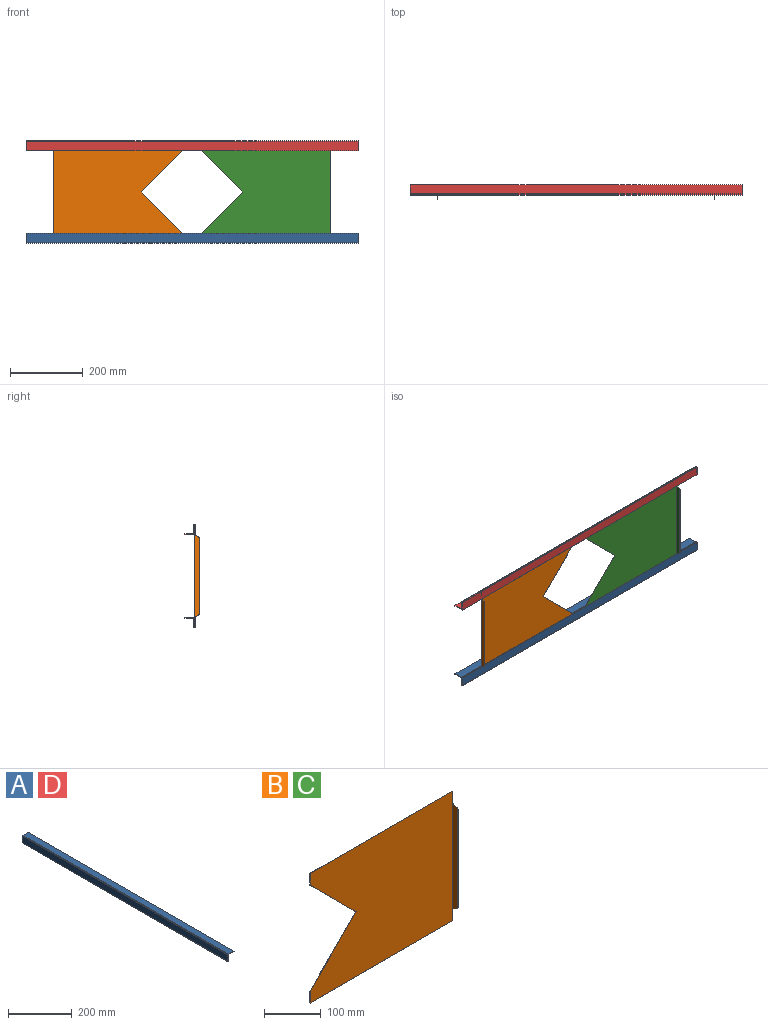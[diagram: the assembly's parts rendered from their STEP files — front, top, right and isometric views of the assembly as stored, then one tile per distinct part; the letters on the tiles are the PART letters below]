
ASSEMBLY  parts=4 mates=9
PART A: 15 faces, bbox 28.3x914.4x27 mm
  f0: plane 914.4x1.59mm, normal (1,0,0), area 1451.6mm2, adj f1,f9,f10,f11
  f1: plane 914.4x23.88mm, normal (0,0,1), area 21832.2mm2, adj f0,f10,f11,f14
  f2: plane 914.4x23.88mm, normal (-1,0,0), area 21832.2mm2, adj f3,f10,f11,f14
  f3: plane 914.4x1.27mm, normal (0,0,1), area 1161.3mm2, adj f2,f4,f10,f11
  f4: plane 914.4x25.4mm, normal (1,0,0), area 23225.8mm2, adj f3,f5,f10,f11
  f5: plane 914.4x1.59mm, normal (0,0,1), area 1451.6mm2, adj f4,f6,f10,f11
  f6: plane 914.4x25.46mm, normal (-1,0,0), area 23283.8mm2, adj f5,f10,f11,f13
  f7: plane 914.4x1.4mm, normal (0,0,-1), area 1277.4mm2, adj f10,f11,f12,f13
  f8: plane 914.4x23.88mm, normal (1,0,0), area 21832.2mm2, adj f9,f10,f11,f12
  f9: plane 914.4x23.81mm, normal (0,0,-1), area 21774.1mm2, adj f0,f8,f10,f11
  f10: plane 28.26x26.99mm, normal (0,-1,0), area 124mm2, adj f0,f1,f2,f3,f4,f5,f6,f7
  f11: plane 28.26x26.99mm, normal (0,1,0), area 124mm2, adj f0,f1,f2,f3,f4,f5,f6,f7
  f12: cylinder r=1.52mm len=914.4mm, axis (0,1,0), area 2189mm2, adj f7,f8,f10,f11
  f13: cylinder r=1.52mm len=914.4mm, axis (0,1,0), area 2189mm2, adj f6,f7,f10,f11
  f14: cylinder r=1.52mm len=914.4mm, axis (0,1,0), area 2189mm2, adj f1,f2,f10,f11
PART B: 16 faces, bbox 355.6x13.3x279.4 mm
  f0: plane 228.6x12.7mm, normal (1,0,0), area 2819.2mm2, adj f1,f11,f12,f13,f14,f15
  f1: plane 209.62x0.55mm, normal (0,-1,0), area 115.5mm2, adj f0,f2,f14,f15
  f2: plane 228.6x12.7mm, normal (-1,0,0), area 2819.2mm2, adj f1,f3,f12,f13,f14,f15
  f3: plane 355.6x279.4mm, normal (0,-1,0), area 86164.2mm2, adj f2,f4,f5,f6,f7,f8,f9,f11
  f4: plane 355.6x0.55mm, normal (0,0,-1), area 195.9mm2, adj f3,f9,f10,f11
  f5: plane 355.6x0.55mm, normal (0,0,1), area 195.9mm2, adj f3,f6,f10,f11
  f6: plane 25.4x0.55mm, normal (-1,0,0), area 14mm2, adj f3,f5,f7,f10
  f7: plane 114.3x114.3mm, normal (-0.71,0,-0.71), area 89.1mm2, adj f3,f6,f8,f10
  f8: plane 114.3x114.3mm, normal (-0.71,0,0.71), area 89.1mm2, adj f3,f7,f9,f10
  f9: plane 25.4x0.55mm, normal (-1,0,0), area 14mm2, adj f3,f4,f8,f10
  f10: plane 355.05x279.4mm, normal (0,1,0), area 86136.2mm2, adj f4,f5,f6,f7,f8,f9,f11
  f11: cylinder r=0.55mm len=279.4mm, axis (0,0,1), area 241.9mm2, adj f0,f3,f4,f5,f10
  f12: plane 9.89x4.95mm, normal (0,-0.45,-0.89), area 6.1mm2, adj f0,f2,f3,f15
  f13: plane 9.89x4.95mm, normal (0,-0.45,0.89), area 6.1mm2, adj f0,f2,f3,f14
  f14: cylinder r=5.08mm len=4.54mm, axis (-1,0,0), area 3.1mm2, adj f0,f1,f2,f13
  f15: cylinder r=5.08mm len=4.54mm, axis (1,0,0), area 3.1mm2, adj f0,f1,f2,f12
PART C: same geometry as B
PART D: same geometry as A
PLACE A rot(axis=(0,0,1),90deg) t=(-914.4,-13.49,1.59)mm
PLACE B rot(axis=(0,1,0),180deg) t=(-482.6,-13.49,255.59)mm
PLACE C t=(-431.8,-13.49,-23.81)mm
PLACE D rot(axis=(-0.71,-0.71,0),180deg) t=(0,-13.49,230.19)mm
MATE planar A.f3 <-> B.f5  axis (0,0,1) through (-457.2,-14.13,-23.81)mm
MATE parallel D.f14 <-> C.f0  axis (1,0,0) through (0,-11.97,231.71)mm
MATE planar A.f3 <-> C.f4  axis (0,0,1) through (-457.2,-14.13,-23.81)mm
MATE planar A.f10 <-> D.f11  axis (1,0,0) through (0,-0.03,1.59)mm
MATE planar D.f3 <-> C.f5  axis (0,0,-1) through (-457.2,-14.13,255.59)mm
MATE planar A.f2 <-> C.f10  axis (0,-1,0) through (-457.2,-13.49,-11.87)mm
MATE planar B.f3 <-> C.f3  axis (0,-1,0) through (-681.32,-14.04,115.89)mm
MATE parallel A.f14 <-> B.f0  axis (-1,0,0) through (-914.4,-11.97,0.06)mm
MATE planar D.f6 <-> A.f6  axis (0,-1,0) through (-457.2,-16.35,242.92)mm
